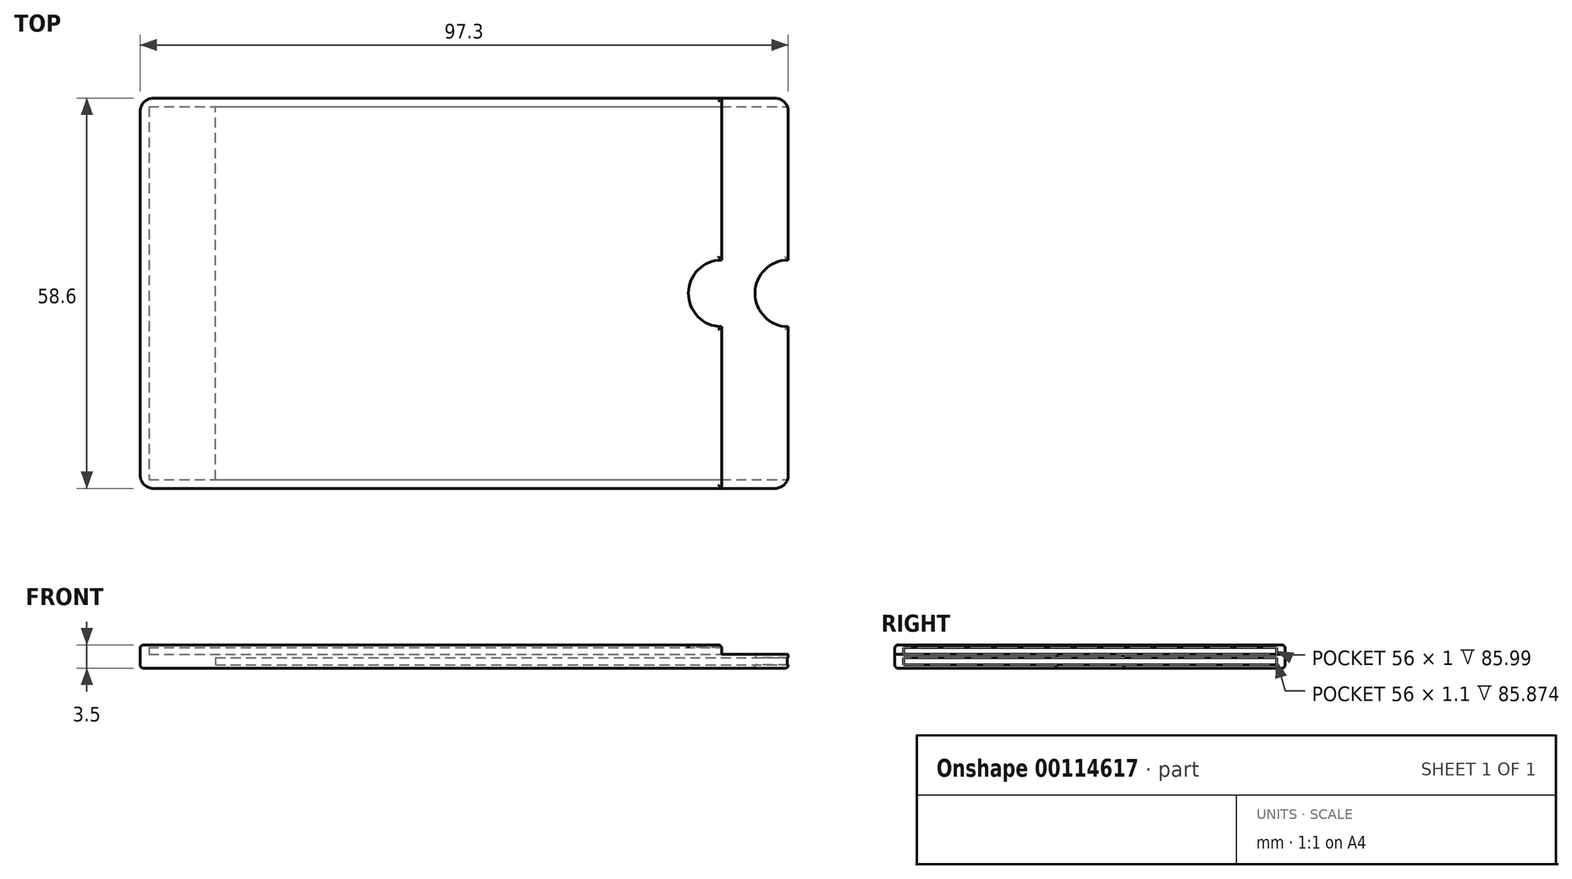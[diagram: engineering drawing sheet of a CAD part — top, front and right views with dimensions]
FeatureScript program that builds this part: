
annotation { "Feature Type Name" : "Feature", "Feature Type Description" : "" }
export const myFeature = defineFeature(function(context is Context, id is Id, definition is map)
    precondition{}
    {
        {
            var Q0;
            Q0=qCreatedBy(makeId("Top.planeOp"),FACE);
            var sketch = newSketch(context, id + "F0", { "sketchPlane" : qUnion([Q0])});
            skLineSegment(sketch, "E0.bottom", {"start": v(-58.38, 43.85) * mm, "end": v(27.62, 43.85) * mm});
            skLineSegment(sketch, "E0.top", {"start": v(-58.38, -12.15) * mm, "end": v(27.62, -12.15) * mm});
            skLineSegment(sketch, "E0.left", {"start": v(-58.38, 43.85) * mm, "end": v(-58.38, -12.15) * mm});
            skLineSegment(sketch, "E0.right", {"start": v(27.62, 45.15) * mm, "end": v(27.62, -13.45) * mm});
            skLineSegment(sketch, "E1.0", {"start": v(-59.68, 45.15) * mm, "end": v(27.62, 45.15) * mm});
            skLineSegment(sketch, "E2.0", {"start": v(-59.68, 45.15) * mm, "end": v(-59.68, -13.45) * mm});
            skLineSegment(sketch, "E3.0", {"start": v(-59.68, -13.45) * mm, "end": v(27.62, -13.45) * mm});
            skArc(sketch, "E4", {"start": v(27.62, 20.85) * mm, "mid": v(22.62, 15.85) * mm, "end": v(27.62, 10.85) * mm});
            skLineSegment(sketch, "E5", {"start": v(-59.68, 15.85) * mm, "end": v(27.62, 15.85) * mm, "construction": true});
            skLineSegment(sketch, "E6", {"start": v(-16.03, 45.15) * mm, "end": v(-16.03, -13.45) * mm, "construction": true});
            skCircle(sketch, "E7", {"center": v(-58.38, -12.15) * mm, "radius": 10 * mm, "construction": true});
            skLineSegment(sketch, "E8", {"start": v(-48.38, -12.15) * mm, "end": v(-48.38, 43.85) * mm});
            skLineSegment(sketch, "E9", {"start": v(27.62, -13.45) * mm, "end": v(37.62, -13.45) * mm, "construction": true});
            skLineSegment(sketch, "E10", {"start": v(37.62, -13.45) * mm, "end": v(37.62, 45.15) * mm});
            skLineSegment(sketch, "E11", {"start": v(37.62, 45.15) * mm, "end": v(27.62, 45.15) * mm, "construction": true});
            skLineSegment(sketch, "E12", {"start": v(27.62, 43.85) * mm, "end": v(37.62, 43.85) * mm});
            skLineSegment(sketch, "E13", {"start": v(27.62, -12.15) * mm, "end": v(37.62, -12.15) * mm});
            skSolve(sketch);
        }
        {
            var Q0;
            {var subQ1=sQuery(id+"F0.wireOp",EDGE,"E0.bottom");Q0=makeQuery(id+"F0.imprint","IMPRINT",FACE,{"disambiguationData":[TD([[makeQuery(id+"F0.imprint","IMPRINT",EDGE,{"derivedFrom":subQ1}),1.0]])]});}
            var Q1;
            {var subQ1=sQuery(id+"F0.wireOp",EDGE,"E0.bottom");Q1=makeQuery(id+"F0.imprint","IMPRINT",FACE,{"disambiguationData":[TD([[makeQuery(id+"F0.imprint","IMPRINT",EDGE,{"derivedFrom":subQ1}),-1.0]])]});}
            var Q2;
            {var subQ3=sQuery(id+"F0.wireOp",EDGE,"E4");Q2=makeQuery(id+"F0.imprint","IMPRINT",FACE,{"disambiguationData":[TD([[makeQuery(id+"F0.imprint","IMPRINT",EDGE,{"derivedFrom":subQ3}),-1.0]])]});}
            extrude(context, id + "F1", {"entities" : qUnion([Q0, Q1, Q2]), "depth" : 3 * mm});
        }
        {
            var Q0;
            {var subQ1=sQuery(id+"F0.wireOp",EDGE,"E0.bottom");Q0=makeQuery(id+"F0.imprint","IMPRINT",FACE,{"disambiguationData":[TD([[makeQuery(id+"F0.imprint","IMPRINT",EDGE,{"derivedFrom":subQ1}),-1.0]])]});}
            var Q1;
            {var subQ3=sQuery(id+"F0.wireOp",EDGE,"E4");Q1=makeQuery(id+"F0.imprint","IMPRINT",FACE,{"disambiguationData":[TD([[makeQuery(id+"F0.imprint","IMPRINT",EDGE,{"derivedFrom":subQ3}),-1.0]])]});}
            extrude(context, id + "F2", {"entities" : qUnion([Q0, Q1]), "operationType" : NewBodyOperationType.REMOVE, "depth" : 2.6 * mm});
        }
        {
            var Q0;
            Q0=qCreatedBy(makeId("Top.planeOp"),FACE);
            var sketch = newSketch(context, id + "F3", { "sketchPlane" : qUnion([Q0])});
            skLineSegment(sketch, "E14.0", {"start": v(37.62, 45.15) * mm, "end": v(37.62, -13.45) * mm});
            skLineSegment(sketch, "E15", {"start": v(37.62, 45.15) * mm, "end": v(27.62, 45.15) * mm});
            skLineSegment(sketch, "E16", {"start": v(37.62, -13.45) * mm, "end": v(27.62, -13.45) * mm});
            skLineSegment(sketch, "E17", {"start": v(27.62, 45.15) * mm, "end": v(27.62, -13.45) * mm});
            skLineSegment(sketch, "E18", {"start": v(27.62, 15.85) * mm, "end": v(37.62, 15.85) * mm, "construction": true});
            skArc(sketch, "E19", {"start": v(37.62, 20.85) * mm, "mid": v(32.62, 15.85) * mm, "end": v(37.62, 10.85) * mm});
            skSolve(sketch);
        }
        {
            var Q0;
            {var subQ3=sQuery(id+"F0.wireOp",EDGE,"E4");Q0=makeQuery(id+"F0.imprint","IMPRINT",FACE,{"disambiguationData":[TD([[makeQuery(id+"F0.imprint","IMPRINT",EDGE,{"derivedFrom":subQ3}),-1.0]])]});}
            var Q1;
            {var subQ0=sQuery(id+"F3.wireOp",EDGE,"E15");Q1=makeQuery(id+"F3.imprint","IMPRINT",FACE,{"disambiguationData":[TD([[makeQuery(id+"F3.imprint","IMPRINT",EDGE,{"derivedFrom":subQ0}),1.0]])]});}
            var Q2;
            {var subQ0=sQuery(id+"F0.wireOp",EDGE,"E4");Q2=makeQuery(id+"F0.imprint","IMPRINT",FACE,{"disambiguationData":[TD([[makeQuery(id+"F0.imprint","IMPRINT",EDGE,{"derivedFrom":subQ0}),1.0]])]});}
            var Q3;
            {var subQ0=sQuery(id+"F0.wireOp",EDGE,"E0.left");Q3=makeQuery(id+"F0.imprint","IMPRINT",FACE,{"disambiguationData":[TD([[makeQuery(id+"F0.imprint","IMPRINT",EDGE,{"derivedFrom":subQ0}),1.0]])]});}
            extrude(context, id + "F4", {"entities" : qUnion([Q0, Q1, Q2, Q3]), "operationType" : NewBodyOperationType.ADD, "depth" : 1.6 * mm});
        }
        {
            var Q0;
            {var subQ0=sQuery(id+"F0.wireOp",EDGE,"E12");Q0=makeQuery(id+"F0.imprint","IMPRINT",FACE,{"disambiguationData":[TD([[makeQuery(id+"F0.imprint","IMPRINT",EDGE,{"derivedFrom":subQ0}),-1.0]])]});}
            var Q1;
            {var subQ3=sQuery(id+"F0.wireOp",EDGE,"E4");Q1=makeQuery(id+"F0.imprint","IMPRINT",FACE,{"disambiguationData":[TD([[makeQuery(id+"F0.imprint","IMPRINT",EDGE,{"derivedFrom":subQ3}),-1.0]])]});}
            var Q2;
            {var subQ0=sQuery(id+"F0.wireOp",EDGE,"E4");Q2=makeQuery(id+"F0.imprint","IMPRINT",FACE,{"disambiguationData":[TD([[makeQuery(id+"F0.imprint","IMPRINT",EDGE,{"derivedFrom":subQ0}),1.0]])]});}
            extrude(context, id + "F5", {"entities" : qUnion([Q0, Q1, Q2]), "operationType" : NewBodyOperationType.REMOVE, "depth" : 1.1 * mm});
        }
        {
            var Q0;
            {var subQ3=sQuery(id+"F0.wireOp",EDGE,"E4");Q0=makeQuery(id+"F0.imprint","IMPRINT",FACE,{"disambiguationData":[TD([[makeQuery(id+"F0.imprint","IMPRINT",EDGE,{"derivedFrom":subQ3}),-1.0]])]});}
            var Q1;
            {var subQ0=sQuery(id+"F0.wireOp",EDGE,"E4");Q1=makeQuery(id+"F0.imprint","IMPRINT",FACE,{"disambiguationData":[TD([[makeQuery(id+"F0.imprint","IMPRINT",EDGE,{"derivedFrom":subQ0}),1.0]])]});}
            var Q2;
            {var subQ0=sQuery(id+"F0.wireOp",EDGE,"E0.left");Q2=makeQuery(id+"F0.imprint","IMPRINT",FACE,{"disambiguationData":[TD([[makeQuery(id+"F0.imprint","IMPRINT",EDGE,{"derivedFrom":subQ0}),1.0]])]});}
            var Q3;
            {var subQ0=sQuery(id+"F3.wireOp",EDGE,"E15");Q3=makeQuery(id+"F3.imprint","IMPRINT",FACE,{"disambiguationData":[TD([[makeQuery(id+"F3.imprint","IMPRINT",EDGE,{"derivedFrom":subQ0}),1.0]])]});}
            var Q4;
            {var subQ6=sQuery(id+"F0.wireOp",EDGE,"E0.left");Q4=makeQuery(id+"F0.imprint","IMPRINT",FACE,{"disambiguationData":[TD([[makeQuery(id+"F0.imprint","IMPRINT",EDGE,{"derivedFrom":subQ6}),-1.0]])]});}
            extrude(context, id + "F6", {"entities" : qUnion([Q0, Q1, Q2, Q3, Q4]), "operationType" : NewBodyOperationType.ADD, "oppositeDirection" : true, "depth" : 0.5 * mm});
        }
        {
            var Q0;
            {var subQ0=sQuery(id+"F0.wireOp",EDGE,"E2.0");var subQ1=sQuery(id+"F0.wireOp",EDGE,"E1.0");Q0=makeQuery(id+"F6.boolean.opBoolean","MERGE",EDGE,{"derivedFrom":[makeQuery(id+"F1.opExtrude","SWEPT_EDGE",EDGE,{"disambiguationData":[OSD([subQ1,subQ0])]}),makeQuery(id+"F6.opExtrude","SWEPT_EDGE",EDGE,{"disambiguationData":[OSD([subQ1,subQ0])]})]});}
            var Q1;
            {var subQ0=sQuery(id+"F0.wireOp",EDGE,"E3.0");var subQ1=sQuery(id+"F0.wireOp",EDGE,"E2.0");Q1=makeQuery(id+"F6.boolean.opBoolean","MERGE",EDGE,{"derivedFrom":[makeQuery(id+"F1.opExtrude","SWEPT_EDGE",EDGE,{"disambiguationData":[OSD([subQ1,subQ0])]}),makeQuery(id+"F6.opExtrude","SWEPT_EDGE",EDGE,{"disambiguationData":[OSD([subQ1,subQ0])]})]});}
            var Q2;
            {var subQ0=sQuery(id+"F3.wireOp",EDGE,"E16");var subQ1=sQuery(id+"F3.wireOp",EDGE,"E14.0");Q2=makeQuery(id+"F6.boolean.opBoolean","MERGE",EDGE,{"derivedFrom":[makeQuery(id+"F4.opExtrude","SWEPT_EDGE",EDGE,{"disambiguationData":[OSD([subQ1,subQ0])]}),makeQuery(id+"F6.opExtrude","SWEPT_EDGE",EDGE,{"disambiguationData":[OSD([subQ1,subQ0])]})]});}
            var Q3;
            {var subQ0=sQuery(id+"F3.wireOp",EDGE,"E15");var subQ1=sQuery(id+"F3.wireOp",EDGE,"E14.0");Q3=makeQuery(id+"F6.boolean.opBoolean","MERGE",EDGE,{"derivedFrom":[makeQuery(id+"F4.opExtrude","SWEPT_EDGE",EDGE,{"disambiguationData":[OSD([subQ1,subQ0])]}),makeQuery(id+"F6.opExtrude","SWEPT_EDGE",EDGE,{"disambiguationData":[OSD([subQ1,subQ0])]})]});}
            fillet(context, id + "F7", {"entities" : qUnion([Q0, Q1, Q2, Q3]), "radius" : 2 * mm, "tangentPropagation" : true, "allowEdgeOverflow" : false});
        }
        {
            var Q0;
            Q0=makeQuery(id+"F1.opExtrude","CAP_EDGE",EDGE,{"disambiguationData":[OSD([sQuery(id+"F0.wireOp",EDGE,"E1.0")])],"isStart":false});
            var Q1;
            Q1=makeQuery(id+"F1.opExtrude","CAP_EDGE",EDGE,{"disambiguationData":[OSD([sQuery(id+"F0.wireOp",EDGE,"E2.0")])],"isStart":false});
            var Q2;
            {var subQ0=sQuery(id+"F0.wireOp",EDGE,"E2.0");var subQ1=sQuery(id+"F0.wireOp",EDGE,"E1.0");Q2=makeQuery(id+"F7.opFillet","BLEND_EDGE",EDGE,{"blendedFrom":[makeQuery(id+"F6.boolean.opBoolean","MERGE",EDGE,{"derivedFrom":[makeQuery(id+"F1.opExtrude","SWEPT_EDGE",EDGE,{"disambiguationData":[OSD([subQ1,subQ0])]}),makeQuery(id+"F6.opExtrude","SWEPT_EDGE",EDGE,{"disambiguationData":[OSD([subQ1,subQ0])]})]}),makeQuery(id+"F1.opExtrude","CAP_FACE",FACE,{"disambiguationData":[OSD([sQuery(id+"F0.wireOp",EDGE,"E0.right"),subQ1,subQ0,sQuery(id+"F0.wireOp",EDGE,"E3.0"),sQuery(id+"F0.wireOp",EDGE,"E4")])],"isStart":false})],"blendedInto":[makeQuery(id+"F1.opExtrude","CAP_FACE",FACE,{"disambiguationData":[OSD([sQuery(id+"F0.wireOp",EDGE,"E0.right"),subQ1,subQ0,sQuery(id+"F0.wireOp",EDGE,"E3.0"),sQuery(id+"F0.wireOp",EDGE,"E4")])],"isStart":false})]});}
            var Q3;
            Q3=makeQuery(id+"F1.opExtrude","CAP_FACE",FACE,{"disambiguationData":[OSD([sQuery(id+"F0.wireOp",EDGE,"E0.right"),sQuery(id+"F0.wireOp",EDGE,"E1.0"),sQuery(id+"F0.wireOp",EDGE,"E2.0"),sQuery(id+"F0.wireOp",EDGE,"E3.0"),sQuery(id+"F0.wireOp",EDGE,"E4")])],"isStart":false});
            var Q4;
            Q4=makeQuery(id+"F6.boolean.opBoolean","MERGE",FACE,{"derivedFrom":[makeQuery(id+"F6.opExtrude","CAP_FACE",FACE,{"disambiguationData":[OSD([sQuery(id+"F0.wireOp",EDGE,"E0.right"),sQuery(id+"F0.wireOp",EDGE,"E1.0"),sQuery(id+"F0.wireOp",EDGE,"E2.0"),sQuery(id+"F0.wireOp",EDGE,"E3.0")])],"isStart":false}),makeQuery(id+"F6.opExtrude","CAP_FACE",FACE,{"disambiguationData":[OSD([sQuery(id+"F3.wireOp",EDGE,"E14.0"),sQuery(id+"F3.wireOp",EDGE,"E15"),sQuery(id+"F3.wireOp",EDGE,"E16"),sQuery(id+"F3.wireOp",EDGE,"E17"),sQuery(id+"F3.wireOp",EDGE,"E19")])],"isStart":false})]});
            fillet(context, id + "F8", {"entities" : qUnion([Q0, Q1, Q2, Q3, Q4]), "radius" : 0.5 * mm, "tangentPropagation" : true, "allowEdgeOverflow" : false});
        }
    });
